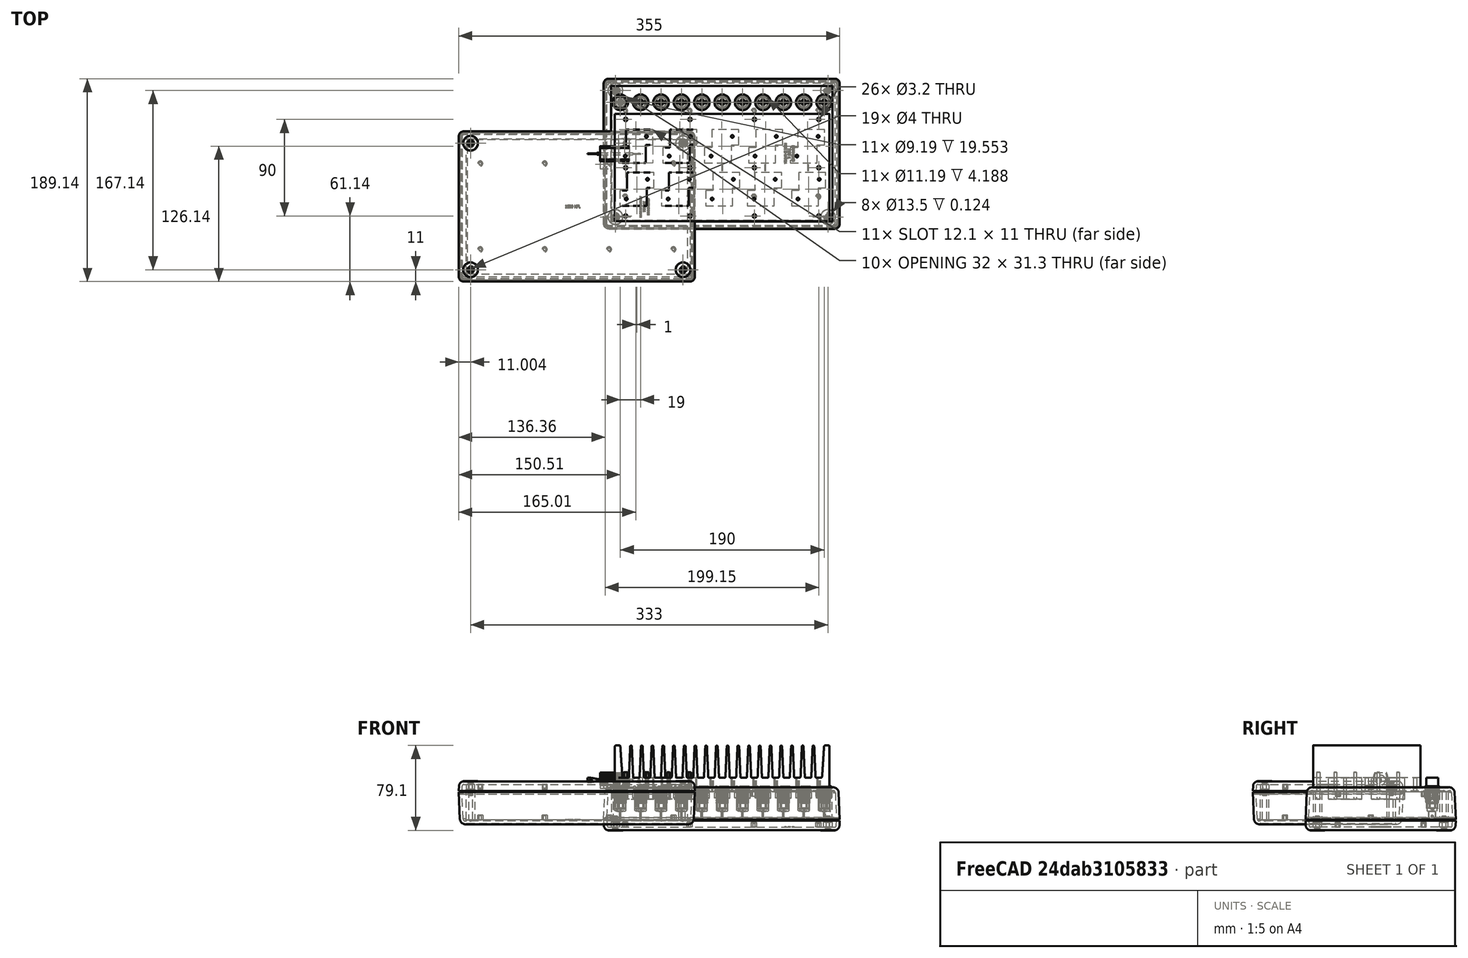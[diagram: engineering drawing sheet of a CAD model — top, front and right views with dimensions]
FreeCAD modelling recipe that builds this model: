
FCSTD DOCUMENT  (FreeCAD 0.20R29410 (Git))
Label: LiPoKiller - Kopie
License: All rights reserved
LicenseURL: http://en.wikipedia.org/wiki/All_rights_reserved
objects: Part::Feature×32, Part::FeaturePython×17, Sketcher::SketchObject×10, Part::Extrusion×10, App::Part×6, Part::MultiFuse×4, Part::Cut×3, App::DocumentObjectGroup×2, Spreadsheet::Sheet×1, PartDesign::CoordinateSystem×1, App::FeaturePython×1
note: 62 computed .brp shape members not serialized (recipe doc carries the construction recipe); baked Part::Feature solids carry a one-line shape summary decoded from their .brp

FEATURE [Spreadsheet::Sheet] Spreadsheet  label="Param"
  cells = A1=R_Grid_Along; B1(R_Grid_Along)=40; A2=R_Grid_Across; B2(R_Grid_Across)=40; A3=R_nof_Along; B3(R_nof_Along)=2; A4=R_nof_Across; B4(R_nof_Across)=5; A5=R_Offset; B5(R_Offset)=1; A6=R_Body_Length; B6(R_Body_Length)=27.3; A7=R_Body_Width; B7(R_Body_Width)=14.2; A8=R_Tab_Length; B8(R_Tab_Length)=10.4; A9=R_Tab_Width; B9(R_Tab_Width)==(28 - 14.2) / 2; A10=R_Clearance; B10(R_Clearance)=2; A11=R_Hole_Along; B11(R_Hole_Along)=18.3; A12=R_Hole_Across; B12(R_Hole_Across)=19.8; A13=R_Hole_Size; B13(R_Hole_Size)=2.5; A14=R_Thread; B14(R_Thread)=M3; A15=Heatsink_Length; B15(Heatsink_Length)=200; A16=Heatsing_Width; B16(Heatsink_Width)=100; A17=Heatsink_Shift; B17(Heatsink_Shift)==26 / 2; A18=Con_Grid; B18(Con_Grid)=19; A19=Con_Pos_y; B19(Con_Pos_y)=48; A20=Con_nof; B20(Con_nof)=11; A21=Con_Diameter; B21(Con_Diameter)=12.1; A22=Con_Width; B22(Con_Width)=11; A23=Heatsink_Hole; B23(Heatsink_Hole)=3.2; C23=Change to 2.5 before manufacturing heatsink; A24=Heatsink_Thread_Hole; B24(Heatsink_Thread_Hole)=2.5; A25=Heatsink_Thread; B25(Heatsink_Thread)=M3; A26=Heatsink_Hole_nof_x; B26(Heatsink_Hole_nof_x)=4; A27=Heatsink_Hole_nof_y; B27(Heatsink_Hole_nof_y)=3; A28=Heatsink_Hole_Grid_x; B28(Heatsink_Hole_Grid_x)=60; A29=Heatsink_Hole_Grid_y; B29(Heatsink_Hole_Grid_y)=45; A30=Heatsink_Hole_Offset; B30(Heatsink_Hole_Offset)=5
FEATURE [Sketcher::SketchObject] Sketch
  FullyConstrained = true
  expr: Constraints[10] = <<Param>>.R_Tab_Width
  expr: Constraints[11] = <<Param>>.R_Tab_Width
  expr: Constraints[12] = <<Param>>.R_Tab_Length + 2 * <<Param>>.R_Clearance
  expr: Constraints[13] = <<Param>>.R_Tab_Length + 2 * <<Param>>.R_Clearance
  expr: Constraints[20] = <<Param>>.R_Grid_Along * (<<Param>>.R_nof_Along - 1) / 2 + <<Param>>.Heatsink_Shift
  expr: Constraints[29] = <<Param>>.Heatsink_Length / 2 - <<Param>>.R_Grid_Across * (<<Param>>.R_nof_Across - 1) / 2 + <<Param>>.R_Offset / 2
  expr: Constraints[8] = Spreadsheet.R_Body_Width + 2 * <<Param>>.R_Clearance
  expr: Constraints[9] = <<Param>>.R_Body_Length + 2 * <<Param>>.R_Clearance
  sketch-geometry (11):
    g0: LineSegment StartX=4.5 StartY=-48.65 StartZ=0 EndX=29.6 EndY=-48.65 EndZ=0
    g1: LineSegment StartX=29.6 StartY=-48.65 StartZ=0 EndX=29.6 EndY=-31.75 EndZ=0
    g2: LineSegment StartX=29.6 StartY=-31.75 StartZ=0 EndX=36.5 EndY=-31.75 EndZ=0
    g3: LineSegment StartX=36.5 StartY=-31.75 StartZ=0 EndX=36.5 EndY=-17.35 EndZ=0
    g4: LineSegment StartX=36.5 StartY=-17.35 StartZ=0 EndX=11.4 EndY=-17.35 EndZ=0
    g5: LineSegment StartX=11.4 StartY=-17.35 StartZ=0 EndX=11.4 EndY=-34.25 EndZ=0
    g6: LineSegment StartX=11.4 StartY=-34.25 StartZ=0 EndX=4.5 EndY=-34.25 EndZ=0
    g7: LineSegment StartX=4.5 StartY=-34.25 StartZ=0 EndX=4.5 EndY=-48.65 EndZ=0
    g8: LineSegment StartX=11.4 StartY=-17.35 StartZ=0 EndX=29.6 EndY=-48.65 EndZ=0
    g9: LineSegment StartX=11.4 StartY=-34.25 StartZ=0 EndX=29.6 EndY=-31.75 EndZ=0
    g10: GeomPoint X=20.5 Y=-33 Z=0
  constraints (30):
    c: Coincident(g0,g1)
    c: Coincident(g1,g2)
    c: Coincident(g2,g3)
    c: Coincident(g3,g4)
    c: Coincident(g4,g5)
    c: Coincident(g5,g6)
    c: Coincident(g6,g7)
    c: Coincident(g7,g0)
    c: Distance(g5,g1) = 18.2
    c: Distance(g4,g0) = 31.3
    c: Distance(g6,g5) = 6.9
    c: Distance(g1,g2) = 6.9
    c: Distance(g3,g2) = 14.4
    c: Distance(g6,g0) = 14.4
    c: Coincident(g8,g4)
    c: Coincident(g9,g5)
    c: Coincident(g9,g1)
    c: Coincident(g8,g0)
    c: PointOnObject(g10,g9)
    c: PointOnObject(g10,g8)
    c: Distance(g10,g-1) = 33
    c: Perpendicular(g0,g7)
    c: Perpendicular(g0,g1)
    c: Perpendicular(g2,g1)
    c: Perpendicular(g2,g3)
    c: Perpendicular(g3,g4)
    c: Perpendicular(g4,g5)
    c: Perpendicular(g5,g6)
    c: Horizontal(g4)
    c: Distance(g10,g-2) = 20.5
FEATURE [Part::Extrusion] Extrude
  Base = -> Sketch
  Dir = (0,0,1)
  DirMode = 2
  FaceMakerClass = Part::FaceMakerBullseye
  LengthFwd = 10
  LengthRev = 10
  Solid = true
  Symmetric = false
FEATURE [Part::FeaturePython] Array001  # Draft array (typed FeaturePython)
  AlwaysSyncPlacement = false
  Angle = 360
  ArrayType = 0
  Axis = (0,0,1)
  Base = -> Extrude
  Center = (0,0,0)
  Count = 3
  ExpandArray = false
  Fuse = false
  IntervalAxis = (0,0,0)
  IntervalX = (80,0,0)
  IntervalY = (0,80,0)
  IntervalZ = (0,0,0)
  NumberCircles = 3
  NumberPolar = 5
  NumberX = 3
  NumberY = 1
  NumberZ = 1
  PlacementList = 3 placements: arithmetic series from (0,0,0) step (80,0,0) to (160,0,0)
  RadialDistance = 50
  ScaleList = (3) [(1,1,1),(1,1,1),(1,1,1)]
  Symmetry = 1
  TangentialDistance = 25
  expr: .IntervalX.x = <<Param>>.R_Grid_Across * 2
  expr: .IntervalY.y = <<Param>>.R_Grid_Along * 2
  expr: NumberX = ceil(<<Param>>.R_nof_Across / 2)
  expr: NumberY = ceil(<<Param>>.R_nof_Along / 2)
FEATURE [Sketcher::SketchObject] Sketch001
  FullyConstrained = true
  expr: Constraints[10] = <<Param>>.R_Tab_Width
  expr: Constraints[11] = <<Param>>.R_Tab_Width
  expr: Constraints[12] = <<Param>>.R_Tab_Length + 2 * <<Param>>.R_Clearance
  expr: Constraints[13] = <<Param>>.R_Tab_Length + 2 * <<Param>>.R_Clearance
  expr: Constraints[20] = <<Param>>.R_Grid_Along * (<<Param>>.R_nof_Along - 1) / 2 + <<Param>>.Heatsink_Shift
  expr: Constraints[29] = <<Param>>.Heatsink_Length / 2 - <<Param>>.R_Grid_Across * (<<Param>>.R_nof_Across - 3) / 2 - <<Param>>.R_Offset / 2
  expr: Constraints[8] = Spreadsheet.R_Body_Width + 2 * <<Param>>.R_Clearance
  expr: Constraints[9] = <<Param>>.R_Body_Length + 2 * <<Param>>.R_Clearance
  sketch-geometry (11):
    g0: LineSegment StartX=43.5 StartY=-48.65 StartZ=0 EndX=68.6 EndY=-48.65 EndZ=0
    g1: LineSegment StartX=68.6 StartY=-48.65 StartZ=0 EndX=68.6 EndY=-31.75 EndZ=0
    g2: LineSegment StartX=68.6 StartY=-31.75 StartZ=0 EndX=75.5 EndY=-31.75 EndZ=0
    g3: LineSegment StartX=75.5 StartY=-31.75 StartZ=0 EndX=75.5 EndY=-17.35 EndZ=0
    g4: LineSegment StartX=75.5 StartY=-17.35 StartZ=0 EndX=50.4 EndY=-17.35 EndZ=0
    g5: LineSegment StartX=50.4 StartY=-17.35 StartZ=0 EndX=50.4 EndY=-34.25 EndZ=0
    g6: LineSegment StartX=50.4 StartY=-34.25 StartZ=0 EndX=43.5 EndY=-34.25 EndZ=0
    g7: LineSegment StartX=43.5 StartY=-34.25 StartZ=0 EndX=43.5 EndY=-48.65 EndZ=0
    g8: LineSegment StartX=50.4 StartY=-17.35 StartZ=0 EndX=68.6 EndY=-48.65 EndZ=0
    g9: LineSegment StartX=50.4 StartY=-34.25 StartZ=0 EndX=68.6 EndY=-31.75 EndZ=0
    g10: GeomPoint X=59.5 Y=-33 Z=0
  constraints (30):
    c: Coincident(g0,g1)
    c: Coincident(g1,g2)
    c: Coincident(g2,g3)
    c: Coincident(g3,g4)
    c: Coincident(g4,g5)
    c: Coincident(g5,g6)
    c: Coincident(g6,g7)
    c: Coincident(g7,g0)
    c: Distance(g5,g1) = 18.2
    c: Distance(g4,g0) = 31.3
    c: Distance(g6,g5) = 6.9
    c: Distance(g1,g2) = 6.9
    c: Distance(g3,g2) = 14.4
    c: Distance(g6,g0) = 14.4
    c: Coincident(g8,g4)
    c: Coincident(g9,g5)
    c: Coincident(g9,g1)
    c: Coincident(g8,g0)
    c: PointOnObject(g10,g9)
    c: PointOnObject(g10,g8)
    c: Distance(g10,g-1) = 33
    c: Perpendicular(g0,g7)
    c: Perpendicular(g0,g1)
    c: Perpendicular(g2,g1)
    c: Perpendicular(g2,g3)
    c: Perpendicular(g3,g4)
    c: Perpendicular(g4,g5)
    c: Perpendicular(g5,g6)
    c: Horizontal(g4)
    c: Distance(g10,g-2) = 59.5
FEATURE [Part::Extrusion] Extrude001
  Base = -> Sketch001
  Dir = (0,0,1)
  DirMode = 2
  FaceMakerClass = Part::FaceMakerBullseye
  LengthFwd = 10
  LengthRev = 10
  Solid = true
  Symmetric = false
FEATURE [Part::FeaturePython] Array002  # Draft array (typed FeaturePython)
  AlwaysSyncPlacement = false
  Angle = 360
  ArrayType = 0
  Axis = (0,0,1)
  Base = -> Extrude001
  Center = (0,0,0)
  Count = 2
  ExpandArray = false
  Fuse = false
  IntervalAxis = (0,0,0)
  IntervalX = (80,0,0)
  IntervalY = (0,80,0)
  IntervalZ = (0,0,0)
  NumberCircles = 3
  NumberPolar = 5
  NumberX = 2
  NumberY = 1
  NumberZ = 1
  PlacementList = 2 placements: [(0,0,0),(80,0,0)]
  RadialDistance = 50
  ScaleList = (2) [(1,1,1),(1,1,1)]
  Symmetry = 1
  TangentialDistance = 25
  expr: .IntervalX.x = <<Param>>.R_Grid_Across * 2
  expr: .IntervalY.y = <<Param>>.R_Grid_Along * 2
  expr: NumberX = floor(<<Param>>.R_nof_Across / 2)
  expr: NumberY = floor(<<Param>>.R_nof_Along / 2)
FEATURE [Sketcher::SketchObject] Sketch002
  FullyConstrained = true
  expr: Constraints[10] = <<Param>>.R_Tab_Width
  expr: Constraints[11] = <<Param>>.R_Tab_Width
  expr: Constraints[12] = <<Param>>.R_Tab_Length + 2 * <<Param>>.R_Clearance
  expr: Constraints[13] = <<Param>>.R_Tab_Length + 2 * <<Param>>.R_Clearance
  expr: Constraints[28] = <<Param>>.Heatsink_Length / 2 - <<Param>>.R_Grid_Across * (<<Param>>.R_nof_Across - 1) / 2 - <<Param>>.R_Offset / 2
  expr: Constraints[31] = <<Param>>.R_Grid_Along * (<<Param>>.R_nof_Along - 1) / 2 + <<Param>>.Heatsink_Shift
  expr: Constraints[33] = <<Param>>.R_Grid_Along
  expr: Constraints[8] = Spreadsheet.R_Body_Width + 2 * <<Param>>.R_Clearance
  expr: Constraints[9] = <<Param>>.R_Body_Length + 2 * <<Param>>.R_Clearance
  sketch-geometry (12):
    g0: LineSegment StartX=3.5 StartY=-8.65 StartZ=0 EndX=28.6 EndY=-8.65 EndZ=0
    g1: LineSegment StartX=28.6 StartY=-8.65 StartZ=0 EndX=28.6 EndY=8.25 EndZ=0
    g2: LineSegment StartX=28.6 StartY=8.25 StartZ=0 EndX=35.5 EndY=8.25 EndZ=0
    g3: LineSegment StartX=35.5 StartY=8.25 StartZ=0 EndX=35.5 EndY=22.65 EndZ=0
    g4: LineSegment StartX=35.5 StartY=22.65 StartZ=0 EndX=10.4 EndY=22.65 EndZ=0
    g5: LineSegment StartX=10.4 StartY=22.65 StartZ=0 EndX=10.4 EndY=5.75 EndZ=0
    g6: LineSegment StartX=10.4 StartY=5.75 StartZ=0 EndX=3.5 EndY=5.75 EndZ=0
    g7: LineSegment StartX=3.5 StartY=5.75 StartZ=0 EndX=3.5 EndY=-8.65 EndZ=0
    g8: LineSegment StartX=10.4 StartY=22.65 StartZ=0 EndX=28.6 EndY=-8.65 EndZ=0
    g9: LineSegment StartX=10.4 StartY=5.75 StartZ=0 EndX=28.6 EndY=8.25 EndZ=0
    g10: GeomPoint X=19.5 Y=7 Z=0
    g11: LineSegment StartX=0 StartY=-33 StartZ=0 EndX=200 EndY=-33 EndZ=0
  constraints (34):
    c: Coincident(g0,g1)
    c: Coincident(g1,g2)
    c: Coincident(g2,g3)
    c: Coincident(g3,g4)
    c: Coincident(g4,g5)
    c: Coincident(g5,g6)
    c: Coincident(g6,g7)
    c: Coincident(g7,g0)
    c: Distance(g5,g1) = 18.2
    c: Distance(g4,g0) = 31.3
    c: Distance(g6,g5) = 6.9
    c: Distance(g1,g2) = 6.9
    c: Distance(g3,g2) = 14.4
    c: Distance(g6,g0) = 14.4
    c: Coincident(g8,g4)
    c: Coincident(g9,g5)
    c: Coincident(g9,g1)
    c: Coincident(g8,g0)
    c: PointOnObject(g10,g9)
    c: PointOnObject(g10,g8)
    c: Perpendicular(g0,g7)
    c: Perpendicular(g0,g1)
    c: Perpendicular(g2,g1)
    c: Perpendicular(g2,g3)
    c: Perpendicular(g3,g4)
    c: Perpendicular(g4,g5)
    c: Perpendicular(g5,g6)
    c: Horizontal(g4)
    c: Distance(g10,g-2) = 19.5
    c: PointOnObject(g11,g-2)
    c: Horizontal(g11)
    c: Distance(g11,g-1) = 33
    c: Distance(g11,g-2) = 200
    c: Distance(g10,g11) = 40
FEATURE [Part::Extrusion] Extrude002
  Base = -> Sketch002
  Dir = (0,0,1)
  DirMode = 2
  FaceMakerClass = Part::FaceMakerBullseye
  LengthFwd = 10
  LengthRev = 10
  Solid = true
  Symmetric = false
FEATURE [Part::FeaturePython] Array003  # Draft array (typed FeaturePython)
  AlwaysSyncPlacement = false
  Angle = 360
  ArrayType = 0
  Axis = (0,0,1)
  Base = -> Extrude002
  Center = (0,0,0)
  Count = 3
  ExpandArray = false
  Fuse = false
  IntervalAxis = (0,0,0)
  IntervalX = (80,0,0)
  IntervalY = (0,80,0)
  IntervalZ = (0,0,0)
  NumberCircles = 3
  NumberPolar = 5
  NumberX = 3
  NumberY = 1
  NumberZ = 1
  PlacementList = 3 placements: arithmetic series from (0,0,0) step (80,0,0) to (160,0,0)
  RadialDistance = 50
  ScaleList = (3) [(1,1,1),(1,1,1),(1,1,1)]
  Symmetry = 1
  TangentialDistance = 25
  expr: .IntervalX.x = <<Param>>.R_Grid_Across * 2
  expr: .IntervalY.y = <<Param>>.R_Grid_Along * 2
  expr: NumberX = ceil(<<Param>>.R_nof_Across / 2)
  expr: NumberY = floor(<<Param>>.R_nof_Along / 2)
FEATURE [Sketcher::SketchObject] Sketch003
  FullyConstrained = true
  expr: Constraints[10] = <<Param>>.R_Tab_Width
  expr: Constraints[11] = <<Param>>.R_Tab_Width
  expr: Constraints[12] = <<Param>>.R_Tab_Length + 2 * <<Param>>.R_Clearance
  expr: Constraints[13] = <<Param>>.R_Tab_Length + 2 * <<Param>>.R_Clearance
  expr: Constraints[28] = <<Param>>.Heatsink_Length / 2 - <<Param>>.R_Grid_Across * (<<Param>>.R_nof_Across - 3) / 2 + <<Param>>.R_Offset / 2
  expr: Constraints[31] = <<Param>>.R_Grid_Along * (<<Param>>.R_nof_Along - 1) / 2 + <<Param>>.Heatsink_Shift
  expr: Constraints[33] = <<Param>>.R_Grid_Along
  expr: Constraints[8] = Spreadsheet.R_Body_Width + 2 * <<Param>>.R_Clearance
  expr: Constraints[9] = <<Param>>.R_Body_Length + 2 * <<Param>>.R_Clearance
  sketch-geometry (12):
    g0: LineSegment StartX=44.5 StartY=-8.65 StartZ=0 EndX=69.6 EndY=-8.65 EndZ=0
    g1: LineSegment StartX=69.6 StartY=-8.65 StartZ=0 EndX=69.6 EndY=8.25 EndZ=0
    g2: LineSegment StartX=69.6 StartY=8.25 StartZ=0 EndX=76.5 EndY=8.25 EndZ=0
    g3: LineSegment StartX=76.5 StartY=8.25 StartZ=0 EndX=76.5 EndY=22.65 EndZ=0
    g4: LineSegment StartX=76.5 StartY=22.65 StartZ=0 EndX=51.4 EndY=22.65 EndZ=0
    g5: LineSegment StartX=51.4 StartY=22.65 StartZ=0 EndX=51.4 EndY=5.75 EndZ=0
    g6: LineSegment StartX=51.4 StartY=5.75 StartZ=0 EndX=44.5 EndY=5.75 EndZ=0
    g7: LineSegment StartX=44.5 StartY=5.75 StartZ=0 EndX=44.5 EndY=-8.65 EndZ=0
    g8: LineSegment StartX=51.4 StartY=22.65 StartZ=0 EndX=69.6 EndY=-8.65 EndZ=0
    g9: LineSegment StartX=51.4 StartY=5.75 StartZ=0 EndX=69.6 EndY=8.25 EndZ=0
    g10: GeomPoint X=60.5 Y=7 Z=0
    g11: LineSegment StartX=0 StartY=-33 StartZ=0 EndX=200 EndY=-33 EndZ=0
  constraints (34):
    c: Coincident(g0,g1)
    c: Coincident(g1,g2)
    c: Coincident(g2,g3)
    c: Coincident(g3,g4)
    c: Coincident(g4,g5)
    c: Coincident(g5,g6)
    c: Coincident(g6,g7)
    c: Coincident(g7,g0)
    c: Distance(g5,g1) = 18.2
    c: Distance(g4,g0) = 31.3
    c: Distance(g6,g5) = 6.9
    c: Distance(g1,g2) = 6.9
    c: Distance(g3,g2) = 14.4
    c: Distance(g6,g0) = 14.4
    c: Coincident(g8,g4)
    c: Coincident(g9,g5)
    c: Coincident(g9,g1)
    c: Coincident(g8,g0)
    c: PointOnObject(g10,g9)
    c: PointOnObject(g10,g8)
    c: Perpendicular(g0,g7)
    c: Perpendicular(g0,g1)
    c: Perpendicular(g2,g1)
    c: Perpendicular(g2,g3)
    c: Perpendicular(g3,g4)
    c: Perpendicular(g4,g5)
    c: Perpendicular(g5,g6)
    c: Horizontal(g4)
    c: Distance(g10,g-2) = 60.5
    c: PointOnObject(g11,g-2)
    c: Horizontal(g11)
    c: Distance(g11,g-1) = 33
    c: Distance(g11,g-2) = 200
    c: Distance(g10,g11) = 40
FEATURE [Part::Extrusion] Extrude003
  Base = -> Sketch003
  Dir = (0,0,1)
  DirMode = 2
  FaceMakerClass = Part::FaceMakerBullseye
  LengthFwd = 10
  LengthRev = 10
  Solid = true
  Symmetric = false
FEATURE [Part::FeaturePython] Array004  # Draft array (typed FeaturePython)
  AlwaysSyncPlacement = false
  Angle = 360
  ArrayType = 0
  Axis = (0,0,1)
  Base = -> Extrude003
  Center = (0,0,0)
  Count = 2
  ExpandArray = false
  Fuse = false
  IntervalAxis = (0,0,0)
  IntervalX = (80,0,0)
  IntervalY = (0,80,0)
  IntervalZ = (0,0,0)
  NumberCircles = 3
  NumberPolar = 5
  NumberX = 2
  NumberY = 1
  NumberZ = 1
  PlacementList = 2 placements: [(0,0,0),(80,0,0)]
  RadialDistance = 50
  ScaleList = (2) [(1,1,1),(1,1,1)]
  Symmetry = 1
  TangentialDistance = 25
  expr: .IntervalX.x = <<Param>>.R_Grid_Across * 2
  expr: .IntervalY.y = <<Param>>.R_Grid_Along * 2
  expr: NumberX = floor(<<Param>>.R_nof_Across / 2)
  expr: NumberY = floor(<<Param>>.R_nof_Along / 2)
FEATURE [Part::Feature] Part__Feature012  label="Resistor Arcol HS"
  shape: bbox 27.3 x 28 x 14.8 mm, 83 faces (baked)
FEATURE [Part::Feature] Part__Feature013  label="Resistor Arcol HS001"
  shape: bbox 33.3 x 2.1 x 2.1 mm, 3 faces (baked)
FEATURE [Part::Feature] Part__Feature014  label="Resistor Arcol HS002"
  shape: bbox 8.85 x 0.8 x 4.5 mm, 7 faces (baked)
FEATURE [Part::Feature] Part__Feature015  label="Resistor Arcol HS003"
  shape: bbox 8.85 x 0.8 x 4.5 mm, 7 faces (baked)
FEATURE [Part::Feature] Part__Feature016  label="Resistor Arcol HS004"
  shape: bbox 27.3 x 9.23 x 9.23 mm, 6 faces, 0 solids (baked)
FEATURE [App::Part] Resistor_Arcol_HS  label="Resistor Arcol HS005"
  Group = -> [Part__Feature012,Part__Feature013,Part__Feature014,Part__Feature015,Part__Feature016]
  Origin = -> Origin002
  Placement = pos=(20.5,-33,2.8e-15) rot=(0.707107,0.707107,0;3.14159rad)
  expr: .Placement.Base.x = <<Param>>.Heatsink_Length / 2 - <<Param>>.R_Grid_Across * (<<Param>>.R_nof_Across - 1) / 2 + <<Param>>.R_Offset / 2
  expr: .Placement.Base.y = -(<<Param>>.R_Grid_Along * (<<Param>>.R_nof_Along - 1) / 2 + <<Param>>.Heatsink_Shift)
FEATURE [Part::FeaturePython] Array005  # Draft array (typed FeaturePython)
  AlwaysSyncPlacement = false
  Angle = 360
  ArrayType = 0
  Axis = (0,0,1)
  Base = -> Resistor_Arcol_HS
  Center = (0,0,0)
  Count = 3
  ExpandArray = false
  Fuse = false
  IntervalAxis = (0,0,0)
  IntervalX = (80,0,0)
  IntervalY = (0,80,0)
  IntervalZ = (0,0,0)
  NumberCircles = 3
  NumberPolar = 5
  NumberX = 3
  NumberY = 1
  NumberZ = 1
  PlacementList = 3 placements: arithmetic series from (20.5,-33,2.8e-15) step (80,0,0) to (180.5,-33,2.8e-15)
  RadialDistance = 50
  ScaleList = (3) [(1,1,1),(1,1,1),(1,1,1)]
  Symmetry = 1
  TangentialDistance = 25
  expr: .IntervalX.x = <<Param>>.R_Grid_Across * 2
  expr: .IntervalY.y = <<Param>>.R_Grid_Along * 2
  expr: NumberX = ceil(<<Param>>.R_nof_Across / 2)
  expr: NumberY = ceil(<<Param>>.R_nof_Along / 2)
FEATURE [Part::Feature] Part__Feature017  label="Resistor Arcol HS006"
  shape: bbox 27.3 x 28 x 14.8 mm, 83 faces (baked)
FEATURE [Part::Feature] Part__Feature018  label="Resistor Arcol HS007"
  shape: bbox 33.3 x 2.1 x 2.1 mm, 3 faces (baked)
FEATURE [Part::Feature] Part__Feature019  label="Resistor Arcol HS008"
  shape: bbox 8.85 x 0.8 x 4.5 mm, 7 faces (baked)
FEATURE [Part::Feature] Part__Feature020  label="Resistor Arcol HS009"
  shape: bbox 8.85 x 0.8 x 4.5 mm, 7 faces (baked)
FEATURE [Part::Feature] Part__Feature021  label="Resistor Arcol HS010"
  shape: bbox 27.3 x 9.23 x 9.23 mm, 6 faces, 0 solids (baked)
FEATURE [App::Part] Resistor_Arcol_HS001  label="Resistor Arcol HS011"
  Group = -> [Part__Feature017,Part__Feature018,Part__Feature019,Part__Feature020,Part__Feature021]
  Origin = -> Origin003
  Placement = pos=(59.5,-33,2.8e-15) rot=(0.707107,0.707107,0;3.14159rad)
  expr: .Placement.Base.x = <<Param>>.Heatsink_Length / 2 - <<Param>>.R_Grid_Across * (<<Param>>.R_nof_Across - 3) / 2 - <<Param>>.R_Offset / 2
  expr: .Placement.Base.y = -(<<Param>>.R_Grid_Along * (<<Param>>.R_nof_Along - 1) / 2 + <<Param>>.Heatsink_Shift)
FEATURE [Part::FeaturePython] Array006  # Draft array (typed FeaturePython)
  AlwaysSyncPlacement = false
  Angle = 360
  ArrayType = 0
  Axis = (0,0,1)
  Base = -> Resistor_Arcol_HS001
  Center = (0,0,0)
  Count = 2
  ExpandArray = false
  Fuse = false
  IntervalAxis = (0,0,0)
  IntervalX = (80,0,0)
  IntervalY = (0,80,0)
  IntervalZ = (0,0,0)
  NumberCircles = 3
  NumberPolar = 5
  NumberX = 2
  NumberY = 1
  NumberZ = 1
  PlacementList = 2 placements: [(59.5,-33,2.8e-15),(139.5,-33,2.8e-15)]
  RadialDistance = 50
  ScaleList = (2) [(1,1,1),(1,1,1)]
  Symmetry = 1
  TangentialDistance = 25
  expr: .IntervalX.x = <<Param>>.R_Grid_Across * 2
  expr: .IntervalY.y = <<Param>>.R_Grid_Along * 2
  expr: NumberX = floor(<<Param>>.R_nof_Across / 2)
  expr: NumberY = floor(<<Param>>.R_nof_Along / 2)
FEATURE [Part::Feature] Part__Feature022  label="Resistor Arcol HS012"
  shape: bbox 27.3 x 28 x 14.8 mm, 83 faces (baked)
FEATURE [Part::Feature] Part__Feature023  label="Resistor Arcol HS013"
  shape: bbox 33.3 x 2.1 x 2.1 mm, 3 faces (baked)
FEATURE [Part::Feature] Part__Feature024  label="Resistor Arcol HS014"
  shape: bbox 8.85 x 0.8 x 4.5 mm, 7 faces (baked)
FEATURE [Part::Feature] Part__Feature025  label="Resistor Arcol HS015"
  shape: bbox 8.85 x 0.8 x 4.5 mm, 7 faces (baked)
FEATURE [Part::Feature] Part__Feature026  label="Resistor Arcol HS016"
  shape: bbox 27.3 x 9.23 x 9.23 mm, 6 faces, 0 solids (baked)
FEATURE [App::Part] Resistor_Arcol_HS002  label="Resistor Arcol HS017"
  Group = -> [Part__Feature022,Part__Feature023,Part__Feature024,Part__Feature025,Part__Feature026]
  Origin = -> Origin004
  Placement = pos=(19.5,7,2.8e-15) rot=(0.707107,0.707107,0;3.14159rad)
  expr: .Placement.Base.x = <<Param>>.Heatsink_Length / 2 - <<Param>>.R_Grid_Across * (<<Param>>.R_nof_Across - 1) / 2 - <<Param>>.R_Offset / 2
  expr: .Placement.Base.y = -(<<Param>>.R_Grid_Along * (<<Param>>.R_nof_Along - 1) / 2 + <<Param>>.Heatsink_Shift) + <<Param>>.R_Grid_Along
FEATURE [Part::FeaturePython] Array007  # Draft array (typed FeaturePython)
  AlwaysSyncPlacement = false
  Angle = 360
  ArrayType = 0
  Axis = (0,0,1)
  Base = -> Resistor_Arcol_HS002
  Center = (0,0,0)
  Count = 3
  ExpandArray = false
  Fuse = false
  IntervalAxis = (0,0,0)
  IntervalX = (80,0,0)
  IntervalY = (0,80,0)
  IntervalZ = (0,0,0)
  NumberCircles = 3
  NumberPolar = 5
  NumberX = 3
  NumberY = 1
  NumberZ = 1
  PlacementList = 3 placements: arithmetic series from (19.5,7,2.8e-15) step (80,0,0) to (179.5,7,2.8e-15)
  RadialDistance = 50
  ScaleList = (3) [(1,1,1),(1,1,1),(1,1,1)]
  Symmetry = 1
  TangentialDistance = 25
  expr: .IntervalX.x = <<Param>>.R_Grid_Across * 2
  expr: .IntervalY.y = <<Param>>.R_Grid_Along * 2
  expr: NumberX = ceil(<<Param>>.R_nof_Across / 2)
  expr: NumberY = floor(<<Param>>.R_nof_Along / 2)
FEATURE [Part::Feature] Part__Feature027  label="Resistor Arcol HS018"
  shape: bbox 27.3 x 28 x 14.8 mm, 83 faces (baked)
FEATURE [Part::Feature] Part__Feature028  label="Resistor Arcol HS019"
  shape: bbox 33.3 x 2.1 x 2.1 mm, 3 faces (baked)
FEATURE [Part::Feature] Part__Feature029  label="Resistor Arcol HS020"
  shape: bbox 8.85 x 0.8 x 4.5 mm, 7 faces (baked)
FEATURE [Part::Feature] Part__Feature030  label="Resistor Arcol HS021"
  shape: bbox 8.85 x 0.8 x 4.5 mm, 7 faces (baked)
FEATURE [Part::Feature] Part__Feature031  label="Resistor Arcol HS022"
  shape: bbox 27.3 x 9.23 x 9.23 mm, 6 faces, 0 solids (baked)
FEATURE [App::Part] Resistor_Arcol_HS003  label="Resistor Arcol HS023"
  Group = -> [Part__Feature027,Part__Feature028,Part__Feature029,Part__Feature030,Part__Feature031]
  Origin = -> Origin005
  Placement = pos=(60.5,7,2.8e-15) rot=(0.707107,0.707107,0;3.14159rad)
  expr: .Placement.Base.x = <<Param>>.Heatsink_Length / 2 - <<Param>>.R_Grid_Across * (<<Param>>.R_nof_Across - 3) / 2 + <<Param>>.R_Offset / 2
  expr: .Placement.Base.y = -(<<Param>>.R_Grid_Along * (<<Param>>.R_nof_Along - 1) / 2 + <<Param>>.Heatsink_Shift) + <<Param>>.R_Grid_Along
FEATURE [Part::FeaturePython] Array008  # Draft array (typed FeaturePython)
  AlwaysSyncPlacement = false
  Angle = 360
  ArrayType = 0
  Axis = (0,0,1)
  Base = -> Resistor_Arcol_HS003
  Center = (0,0,0)
  Count = 2
  ExpandArray = false
  Fuse = false
  IntervalAxis = (0,0,0)
  IntervalX = (80,0,0)
  IntervalY = (0,80,0)
  IntervalZ = (0,0,0)
  NumberCircles = 3
  NumberPolar = 5
  NumberX = 2
  NumberY = 1
  NumberZ = 1
  PlacementList = 2 placements: [(60.5,7,2.8e-15),(140.5,7,2.8e-15)]
  RadialDistance = 50
  ScaleList = (2) [(1,1,1),(1,1,1)]
  Symmetry = 1
  TangentialDistance = 25
  expr: .IntervalX.x = <<Param>>.R_Grid_Across * 2
  expr: .IntervalY.y = <<Param>>.R_Grid_Along * 2
  expr: NumberX = floor(<<Param>>.R_nof_Across / 2)
  expr: NumberY = floor(<<Param>>.R_nof_Along / 2)
FEATURE [Part::MultiFuse] Fusion
  Shapes = -> [Array001,Array002,Array003,Array004]
FEATURE [Sketcher::SketchObject] Sketch004
  FullyConstrained = true
  expr: Constraints[10] = <<Param>>.Con_Pos_y
  expr: Constraints[12] = <<Param>>.Heatsink_Length / 2 - <<Param>>.Con_Grid * (<<Param>>.Con_nof - 1) / 2
  expr: Constraints[6] = <<Param>>.Con_Diameter
  expr: Constraints[7] = <<Param>>.Con_Diameter
  expr: Constraints[8] = <<Param>>.Con_Width
  expr: Constraints[9] = <<Param>>.Con_Width / 2
  sketch-geometry (4):
    g0: ArcOfCircle CenterX=5 CenterY=48 CenterZ=0 NormalX=0 NormalY=0 NormalZ=1 AngleXU=0 Radius=6.05 StartAngle=2.0005 EndAngle=4.28269
    g1: ArcOfCircle CenterX=5 CenterY=48 CenterZ=0 NormalX=0 NormalY=0 NormalZ=1 AngleXU=0 Radius=6.05 StartAngle=5.14209 EndAngle=7.42428
    g2: LineSegment StartX=2.47958 StartY=53.5 StartZ=0 EndX=7.52042 EndY=53.5 EndZ=0
    g3: LineSegment StartX=7.52042 StartY=42.5 StartZ=0 EndX=2.47958 EndY=42.5 EndZ=0
  constraints (13):
    c: Coincident(g1,g0)
    c: Coincident(g2,g0)
    c: Coincident(g2,g1)
    c: Coincident(g3,g1)
    c: Coincident(g3,g0)
    c: Horizontal(g3)
    c: Diameter(g1) = 12.1
    c: Diameter(g0) = 12.1
    c: Distance(g1,g3) = 11
    c: Distance(g0,g3) = 5.5
    c: Distance(g0,g-1) = 48
    c: Horizontal(g2)
    c: Distance(g0,g-2) = 5
FEATURE [Part::Extrusion] Extrude004
  Base = -> Sketch004
  Dir = (0,0,1)
  DirMode = 2
  FaceMakerClass = Part::FaceMakerBullseye
  LengthFwd = 10
  LengthRev = 10
  Solid = true
  Symmetric = false
FEATURE [Part::FeaturePython] Array009  # Draft array (typed FeaturePython)
  AlwaysSyncPlacement = false
  Angle = 360
  ArrayType = 0
  Axis = (0,0,1)
  Base = -> Extrude004
  Center = (0,0,0)
  Count = 11
  ExpandArray = false
  Fuse = false
  IntervalAxis = (0,0,0)
  IntervalX = (19,0,0)
  IntervalY = (0,100,0)
  IntervalZ = (0,0,100)
  NumberCircles = 3
  NumberPolar = 5
  NumberX = 11
  NumberY = 1
  NumberZ = 1
  PlacementList = 11 placements: arithmetic series from (0,0,0) step (19,0,0) to (190,0,0)
  RadialDistance = 50
  ScaleList = (11) [(1,1,1),(1,1,1),(1,1,1),(1,1,1),(1,1,1),(1,1,1),(1,1,1),(1,1,1),(1,1,1),(1,1,1),(1,1,1)]
  Symmetry = 1
  TangentialDistance = 25
FEATURE [Part::MultiFuse] Fusion001
  Shapes = -> [Array009,Fusion]
FEATURE [Sketcher::SketchObject] Sketch005
  FullyConstrained = true
  expr: Constraints[12] = <<Param>>.R_Hole_Size
  expr: Constraints[13] = <<Param>>.R_Hole_Size
  expr: Constraints[1] = <<Param>>.R_Grid_Along * (<<Param>>.R_nof_Along - 1) / 2 + <<Param>>.Heatsink_Shift
  expr: Constraints[2] = <<Param>>.Heatsink_Length / 2 - <<Param>>.R_Grid_Across * (<<Param>>.R_nof_Across - 1) / 2 + <<Param>>.R_Offset / 2
  expr: Constraints[5] = <<Param>>.R_Hole_Across
  expr: Constraints[6] = <<Param>>.R_Hole_Along
  sketch-geometry (6):
    g0: LineSegment StartX=30.4 StartY=-23.85 StartZ=0 EndX=10.6 EndY=-42.15 EndZ=0
    g1: GeomPoint X=20.5 Y=-33 Z=0
    g2: Circle CenterX=30.4 CenterY=-23.85 CenterZ=0 NormalX=0 NormalY=0 NormalZ=1 AngleXU=0 Radius=1.25
    g3: Circle CenterX=10.6 CenterY=-42.15 CenterZ=0 NormalX=0 NormalY=0 NormalZ=1 AngleXU=0 Radius=1.25
    g4: LineSegment StartX=20.5 StartY=-33 StartZ=0 EndX=30.4 EndY=-23.85 EndZ=0
    g5: LineSegment StartX=20.5 StartY=-33 StartZ=0 EndX=10.6 EndY=-42.15 EndZ=0
  constraints (14):
    c: PointOnObject(g1,g0)
    c: Distance(g1,g-1) = 33
    c: Distance(g1,g-2) = 20.5
    c: Coincident(g0,g2)
    c: Coincident(g0,g3)
    c: DistanceX(g3,g2) = 19.8
    c: DistanceY(g3,g2) = 18.3
    c: Coincident(g4,g1)
    c: Coincident(g4,g2)
    c: Coincident(g5,g1)
    c: Coincident(g5,g3)
    c: Equal(g4,g5)
    c: Diameter(g2) = 2.5
    c: Diameter(g3) = 2.5
FEATURE [Part::Extrusion] Extrude005
  Base = -> Sketch005
  Dir = (0,0,1)
  DirMode = 2
  FaceMakerClass = Part::FaceMakerBullseye
  LengthFwd = 15
  LengthRev = 10
  Solid = true
  Symmetric = false
FEATURE [Part::FeaturePython] Array010  # Draft array (typed FeaturePython)
  AlwaysSyncPlacement = false
  Angle = 360
  ArrayType = 0
  Axis = (0,0,1)
  Base = -> Extrude005
  Center = (0,0,0)
  Count = 3
  ExpandArray = false
  Fuse = false
  IntervalAxis = (0,0,0)
  IntervalX = (80,0,0)
  IntervalY = (0,80,0)
  IntervalZ = (0,0,0)
  NumberCircles = 3
  NumberPolar = 5
  NumberX = 3
  NumberY = 1
  NumberZ = 1
  PlacementList = 3 placements: arithmetic series from (0,0,0) step (80,0,0) to (160,0,0)
  RadialDistance = 50
  ScaleList = (3) [(1,1,1),(1,1,1),(1,1,1)]
  Symmetry = 1
  TangentialDistance = 25
  expr: .IntervalX.x = <<Param>>.R_Grid_Across * 2
  expr: .IntervalY.y = <<Param>>.R_Grid_Along * 2
  expr: NumberX = ceil(<<Param>>.R_nof_Across / 2)
  expr: NumberY = ceil(<<Param>>.R_nof_Along / 2)
FEATURE [Sketcher::SketchObject] Sketch006
  FullyConstrained = true
  expr: Constraints[12] = <<Param>>.R_Hole_Size
  expr: Constraints[13] = <<Param>>.R_Hole_Size
  expr: Constraints[1] = <<Param>>.R_Grid_Along * (<<Param>>.R_nof_Along - 1) / 2 + <<Param>>.Heatsink_Shift
  expr: Constraints[2] = <<Param>>.Heatsink_Length / 2 - <<Param>>.R_Grid_Across * (<<Param>>.R_nof_Across - 3) / 2 - <<Param>>.R_Offset / 2
  expr: Constraints[5] = <<Param>>.R_Hole_Across
  expr: Constraints[6] = <<Param>>.R_Hole_Along
  sketch-geometry (6):
    g0: LineSegment StartX=69.4 StartY=-23.85 StartZ=0 EndX=49.6 EndY=-42.15 EndZ=0
    g1: GeomPoint X=59.5 Y=-33 Z=0
    g2: Circle CenterX=69.4 CenterY=-23.85 CenterZ=0 NormalX=0 NormalY=0 NormalZ=1 AngleXU=0 Radius=1.25
    g3: Circle CenterX=49.6 CenterY=-42.15 CenterZ=0 NormalX=0 NormalY=0 NormalZ=1 AngleXU=0 Radius=1.25
    g4: LineSegment StartX=59.5 StartY=-33 StartZ=0 EndX=69.4 EndY=-23.85 EndZ=0
    g5: LineSegment StartX=59.5 StartY=-33 StartZ=0 EndX=49.6 EndY=-42.15 EndZ=0
  constraints (14):
    c: PointOnObject(g1,g0)
    c: Distance(g1,g-1) = 33
    c: Distance(g1,g-2) = 59.5
    c: Coincident(g0,g2)
    c: Coincident(g0,g3)
    c: DistanceX(g3,g2) = 19.8
    c: DistanceY(g3,g2) = 18.3
    c: Coincident(g4,g1)
    c: Coincident(g4,g2)
    c: Coincident(g5,g1)
    c: Coincident(g5,g3)
    c: Equal(g4,g5)
    c: Diameter(g2) = 2.5
    c: Diameter(g3) = 2.5
FEATURE [Part::Extrusion] Extrude006
  Base = -> Sketch006
  Dir = (0,0,1)
  DirMode = 2
  FaceMakerClass = Part::FaceMakerBullseye
  LengthFwd = 15
  LengthRev = 10
  Solid = true
  Symmetric = false
FEATURE [Part::FeaturePython] Array011  # Draft array (typed FeaturePython)
  AlwaysSyncPlacement = false
  Angle = 360
  ArrayType = 0
  Axis = (0,0,1)
  Base = -> Extrude006
  Center = (0,0,0)
  Count = 2
  ExpandArray = false
  Fuse = false
  IntervalAxis = (0,0,0)
  IntervalX = (80,0,0)
  IntervalY = (0,80,0)
  IntervalZ = (0,0,0)
  NumberCircles = 3
  NumberPolar = 5
  NumberX = 2
  NumberY = 1
  NumberZ = 1
  PlacementList = 2 placements: [(0,0,0),(80,0,0)]
  RadialDistance = 50
  ScaleList = (2) [(1,1,1),(1,1,1)]
  Symmetry = 1
  TangentialDistance = 25
  expr: .IntervalX.x = <<Param>>.R_Grid_Across * 2
  expr: .IntervalY.y = <<Param>>.R_Grid_Along * 2
  expr: NumberX = floor(<<Param>>.R_nof_Across / 2)
  expr: NumberY = ceil(<<Param>>.R_nof_Along / 2)
FEATURE [Sketcher::SketchObject] Sketch007
  FullyConstrained = true
  expr: Constraints[11] = <<Param>>.R_Hole_Size
  expr: Constraints[12] = <<Param>>.R_Hole_Size
  expr: Constraints[16] = <<Param>>.R_Grid_Along * (<<Param>>.R_nof_Along - 1) / 2 + <<Param>>.Heatsink_Shift
  expr: Constraints[17] = <<Param>>.R_Grid_Along
  expr: Constraints[1] = <<Param>>.Heatsink_Length / 2 - <<Param>>.R_Grid_Across * (<<Param>>.R_nof_Across - 1) / 2 - <<Param>>.R_Offset / 2
  expr: Constraints[4] = <<Param>>.R_Hole_Across
  expr: Constraints[5] = <<Param>>.R_Hole_Along
  sketch-geometry (7):
    g0: LineSegment StartX=29.4 StartY=16.15 StartZ=0 EndX=9.6 EndY=-2.15 EndZ=0
    g1: GeomPoint X=19.5 Y=7 Z=0
    g2: Circle CenterX=29.4 CenterY=16.15 CenterZ=0 NormalX=0 NormalY=0 NormalZ=1 AngleXU=0 Radius=1.25
    g3: Circle CenterX=9.6 CenterY=-2.15 CenterZ=0 NormalX=0 NormalY=0 NormalZ=1 AngleXU=0 Radius=1.25
    g4: LineSegment StartX=19.5 StartY=7 StartZ=0 EndX=29.4 EndY=16.15 EndZ=0
    g5: LineSegment StartX=19.5 StartY=7 StartZ=0 EndX=9.6 EndY=-2.15 EndZ=0
    g6: LineSegment StartX=0 StartY=-33 StartZ=0 EndX=200 EndY=-33 EndZ=0
  constraints (18):
    c: PointOnObject(g1,g0)
    c: Distance(g1,g-2) = 19.5
    c: Coincident(g0,g2)
    c: Coincident(g0,g3)
    c: DistanceX(g3,g2) = 19.8
    c: DistanceY(g3,g2) = 18.3
    c: Coincident(g4,g1)
    c: Coincident(g4,g2)
    c: Coincident(g5,g1)
    c: Coincident(g5,g3)
    c: Equal(g4,g5)
    c: Diameter(g2) = 2.5
    c: Diameter(g3) = 2.5
    c: PointOnObject(g6,g-2)
    c: Horizontal(g6)
    c: Distance(g6,g-2) = 200
    c: Distance(g6,g-1) = 33
    c: Distance(g1,g6) = 40
FEATURE [Part::Extrusion] Extrude007
  Base = -> Sketch007
  Dir = (0,0,1)
  DirMode = 2
  FaceMakerClass = Part::FaceMakerBullseye
  LengthFwd = 15
  LengthRev = 10
  Solid = true
  Symmetric = false
FEATURE [Part::FeaturePython] Array012  # Draft array (typed FeaturePython)
  AlwaysSyncPlacement = false
  Angle = 360
  ArrayType = 0
  Axis = (0,0,1)
  Base = -> Extrude007
  Center = (0,0,0)
  Count = 3
  ExpandArray = false
  Fuse = false
  IntervalAxis = (0,0,0)
  IntervalX = (80,0,0)
  IntervalY = (0,80,0)
  IntervalZ = (0,0,0)
  NumberCircles = 3
  NumberPolar = 5
  NumberX = 3
  NumberY = 1
  NumberZ = 1
  PlacementList = 3 placements: arithmetic series from (0,0,0) step (80,0,0) to (160,0,0)
  RadialDistance = 50
  ScaleList = (3) [(1,1,1),(1,1,1),(1,1,1)]
  Symmetry = 1
  TangentialDistance = 25
  expr: .IntervalX.x = <<Param>>.R_Grid_Across * 2
  expr: .IntervalY.y = <<Param>>.R_Grid_Along * 2
  expr: NumberX = ceil(<<Param>>.R_nof_Across / 2)
  expr: NumberY = floor(<<Param>>.R_nof_Along / 2)
FEATURE [Sketcher::SketchObject] Sketch008
  FullyConstrained = true
  expr: Constraints[11] = <<Param>>.R_Hole_Size
  expr: Constraints[12] = <<Param>>.R_Hole_Size
  expr: Constraints[16] = <<Param>>.R_Grid_Along * (<<Param>>.R_nof_Along - 1) / 2 + <<Param>>.Heatsink_Shift
  expr: Constraints[17] = <<Param>>.R_Grid_Along
  expr: Constraints[1] = <<Param>>.Heatsink_Length / 2 - <<Param>>.R_Grid_Across * (<<Param>>.R_nof_Across - 3) / 2 + <<Param>>.R_Offset / 2
  expr: Constraints[4] = <<Param>>.R_Hole_Across
  expr: Constraints[5] = <<Param>>.R_Hole_Along
  sketch-geometry (7):
    g0: LineSegment StartX=70.4 StartY=16.15 StartZ=0 EndX=50.6 EndY=-2.15 EndZ=0
    g1: GeomPoint X=60.5 Y=7 Z=0
    g2: Circle CenterX=70.4 CenterY=16.15 CenterZ=0 NormalX=0 NormalY=0 NormalZ=1 AngleXU=0 Radius=1.25
    g3: Circle CenterX=50.6 CenterY=-2.15 CenterZ=0 NormalX=0 NormalY=0 NormalZ=1 AngleXU=0 Radius=1.25
    g4: LineSegment StartX=60.5 StartY=7 StartZ=0 EndX=70.4 EndY=16.15 EndZ=0
    g5: LineSegment StartX=60.5 StartY=7 StartZ=0 EndX=50.6 EndY=-2.15 EndZ=0
    g6: LineSegment StartX=0 StartY=-33 StartZ=0 EndX=200 EndY=-33 EndZ=0
  constraints (18):
    c: PointOnObject(g1,g0)
    c: Distance(g1,g-2) = 60.5
    c: Coincident(g0,g2)
    c: Coincident(g0,g3)
    c: DistanceX(g3,g2) = 19.8
    c: DistanceY(g3,g2) = 18.3
    c: Coincident(g4,g1)
    c: Coincident(g4,g2)
    c: Coincident(g5,g1)
    c: Coincident(g5,g3)
    c: Equal(g4,g5)
    c: Diameter(g2) = 2.5
    c: Diameter(g3) = 2.5
    c: PointOnObject(g6,g-2)
    c: Horizontal(g6)
    c: Distance(g6,g-2) = 200
    c: Distance(g6,g-1) = 33
    c: Distance(g1,g6) = 40
FEATURE [Part::Extrusion] Extrude008
  Base = -> Sketch008
  Dir = (0,0,1)
  DirMode = 2
  FaceMakerClass = Part::FaceMakerBullseye
  LengthFwd = 15
  LengthRev = 10
  Solid = true
  Symmetric = false
FEATURE [Part::FeaturePython] Array013  # Draft array (typed FeaturePython)
  AlwaysSyncPlacement = false
  Angle = 360
  ArrayType = 0
  Axis = (0,0,1)
  Base = -> Extrude008
  Center = (0,0,0)
  Count = 2
  ExpandArray = false
  Fuse = false
  IntervalAxis = (0,0,0)
  IntervalX = (80,0,0)
  IntervalY = (0,80,0)
  IntervalZ = (0,0,0)
  NumberCircles = 3
  NumberPolar = 5
  NumberX = 2
  NumberY = 1
  NumberZ = 1
  PlacementList = 2 placements: [(0,0,0),(80,0,0)]
  RadialDistance = 50
  ScaleList = (2) [(1,1,1),(1,1,1)]
  Symmetry = 1
  TangentialDistance = 25
  expr: .IntervalX.x = <<Param>>.R_Grid_Across * 2
  expr: .IntervalY.y = <<Param>>.R_Grid_Along * 2
  expr: NumberX = floor(<<Param>>.R_nof_Across / 2)
  expr: NumberY = floor(<<Param>>.R_nof_Along / 2)
FEATURE [Part::MultiFuse] Fusion002
  Shapes = -> [Array010,Array011,Array012,Array013]
FEATURE [Sketcher::SketchObject] Sketch009
  FullyConstrained = true
  expr: Constraints[0] = <<Param>>.Heatsink_Hole
  expr: Constraints[1] = <<Param>>.Heatsink_Hole_Grid_y * (<<Param>>.Heatsink_Hole_nof_y - 1) / 2 + <<Param>>.Heatsink_Shift
  expr: Constraints[5] = <<Param>>.Heatsink_Hole_Grid_x * (<<Param>>.Heatsink_Hole_nof_x - 1) / 2
  expr: Constraints[6] = <<Param>>.Heatsink_Length / 2
  sketch-geometry (2):
    g0: Circle CenterX=10 CenterY=-58 CenterZ=0 NormalX=0 NormalY=0 NormalZ=1 AngleXU=0 Radius=1.6
    g1: LineSegment StartX=100 StartY=0 StartZ=0 EndX=100 EndY=-100 EndZ=0
  constraints (7):
    c: Diameter(g0) = 3.2
    c: Distance(g0,g-1) = 58
    c: PointOnObject(g1,g-1)
    c: Vertical(g1)
    c: Distance(g1) = 100
    c: Distance(g0,g1) = 90
    c: Distance(g1,g-2) = 100
FEATURE [Part::Extrusion] Extrude009
  Base = -> Sketch009
  Dir = (0,0,1)
  DirMode = 2
  FaceMakerClass = Part::FaceMakerBullseye
  LengthFwd = 15
  LengthRev = 10
  Solid = true
  Symmetric = false
FEATURE [Part::FeaturePython] Array014  # Draft array (typed FeaturePython)
  AlwaysSyncPlacement = false
  Angle = 360
  ArrayType = 0
  Axis = (0,0,1)
  Base = -> Extrude009
  Center = (0,0,0)
  Count = 12
  ExpandArray = false
  Fuse = false
  IntervalAxis = (0,0,0)
  IntervalX = (60,0,0)
  IntervalY = (0,45,0)
  IntervalZ = (0,0,100)
  NumberCircles = 3
  NumberPolar = 5
  NumberX = 4
  NumberY = 3
  NumberZ = 1
  PlacementList = 12 placements: [(0,0,0),(0,45,0),(0,90,0),(60,0,0),(60,45,0),(60,90,0),(120,0,0),(120,45,0),(120,90,0),(180,0,0),(180,45,0),(180,90,0)]
  RadialDistance = 50
  ScaleList = (12) [(1,1,1),(1,1,1),(1,1,1),(1,1,1),(1,1,1),(1,1,1),(1,1,1),(1,1,1),(1,1,1),(1,1,1),(1,1,1),(1,1,1)]
  Symmetry = 1
  TangentialDistance = 25
  expr: .IntervalX.x = <<Param>>.Heatsink_Hole_Grid_x
  expr: .IntervalY.y = <<Param>>.Heatsink_Hole_Grid_y
  expr: NumberX = <<Param>>.Heatsink_Hole_nof_x
  expr: NumberY = <<Param>>.Heatsink_Hole_nof_y
FEATURE [Part::FeaturePython] Array015  # Draft array (typed FeaturePython)
  AlwaysSyncPlacement = false
  Angle = 360
  ArrayType = 0
  Axis = (0,0,1)
  Base = -> Extrude009
  Center = (0,0,0)
  Count = 12
  ExpandArray = false
  Fuse = false
  IntervalAxis = (0,0,0)
  IntervalX = (60,0,0)
  IntervalY = (0,45,0)
  IntervalZ = (0,0,100)
  NumberCircles = 3
  NumberPolar = 5
  NumberX = 4
  NumberY = 3
  NumberZ = 1
  PlacementList = 12 placements: [(0,0,0),(0,45,0),(0,90,0),(60,0,0),(60,45,0),(60,90,0),(120,0,0),(120,45,0),(120,90,0),(180,0,0),(180,45,0),(180,90,0)]
  RadialDistance = 50
  ScaleList = (12) [(1,1,1),(1,1,1),(1,1,1),(1,1,1),(1,1,1),(1,1,1),(1,1,1),(1,1,1),(1,1,1),(1,1,1),(1,1,1),(1,1,1)]
  Symmetry = 1
  TangentialDistance = 25
  expr: .IntervalX.x = <<Param>>.Heatsink_Hole_Grid_x
  expr: .IntervalY.y = <<Param>>.Heatsink_Hole_Grid_y
  expr: NumberX = <<Param>>.Heatsink_Hole_nof_x
  expr: NumberY = <<Param>>.Heatsink_Hole_nof_y
FEATURE [Part::MultiFuse] Fusion003
  Shapes = -> [Fusion002,Array014]
FEATURE [PartDesign::CoordinateSystem] LCS_Origin
  AttacherType = Attacher::AttachEngine3D
  MapMode = 2
  Support = -> [X_Axis001]
FEATURE [App::DocumentObjectGroup] Constraints
FEATURE [Part::Feature] Part__Feature  label="1599K Lid"
  Placement = pos=(-35.5062,-49.1401,-2.40297) rot=(1,0,0;3.14159rad)
  shape: bbox 220 x 140 x 522.1 mm, 504 faces (baked)
FEATURE [Part::Feature] Part__Feature001  label="1599K Box"
  Placement = pos=(-35.5062,-49.1401,-3.40297) rot=(0,0,1;0rad)
  shape: bbox 220 x 140 x 525.6 mm, 228 faces (baked)
FEATURE [Part::Feature] Part__Feature002  label="SC590 (screw M3-0.5X 12mm FH)"
  Placement = pos=(-134.506,9.85994,4.35203) rot=(1,0,0;1.5708rad)
  shape: bbox 5.514 x 5.514 x 12.01 mm, 26 faces (baked)
FEATURE [Part::Feature] Part__Feature003  label="SC590 (screw M3-0.5X 12mm FH)001"
  Placement = pos=(-134.506,-108.14,4.35203) rot=(1,0,0;1.5708rad)
  shape: bbox 5.514 x 5.514 x 12.01 mm, 26 faces (baked)
FEATURE [Part::Feature] Part__Feature004  label="SC590 (screw M3-0.5X 12mm FH)002"
  Placement = pos=(63.4938,9.85994,4.35203) rot=(0.97539,-0.155908,-0.155908;1.59571rad)
  shape: bbox 5.514 x 5.514 x 12.01 mm, 26 faces (baked)
FEATURE [Part::Feature] Part__Feature005  label="SC590 (screw M3-0.5X 12mm FH)003"
  Placement = pos=(63.4938,-108.14,4.35203) rot=(1,0,0;1.5708rad)
  shape: bbox 5.514 x 5.514 x 12.01 mm, 26 faces (baked)
FEATURE [Part::Feature] Part__Feature006  label="IN100 (insert M3-0.5X5.75mm BRASS)"
  Placement = pos=(63.4938,9.85994,-6.61797) rot=(1,0,0;1.5708rad)
  shape: bbox 4.846 x 4.846 x 5.715 mm, 136 faces (baked)
FEATURE [Part::Feature] Part__Feature007  label="IN100 (insert M3-0.5X5.75mm BRASS)001"
  Placement = pos=(-134.506,9.85994,-6.61797) rot=(1,0,0;1.5708rad)
  shape: bbox 4.846 x 4.846 x 5.715 mm, 136 faces (baked)
FEATURE [Part::Feature] Part__Feature008  label="IN100 (insert M3-0.5X5.75mm BRASS)002"
  Placement = pos=(63.4938,-108.14,-6.61797) rot=(1,0,0;1.5708rad)
  shape: bbox 4.846 x 4.846 x 5.715 mm, 136 faces (baked)
FEATURE [Part::Feature] Part__Feature009  label="IN100 (insert M3-0.5X5.75mm BRASS)003"
  Placement = pos=(-134.506,-108.14,-6.61797) rot=(1,0,0;1.5708rad)
  shape: bbox 4.846 x 4.846 x 5.715 mm, 136 faces (baked)
FEATURE [App::Part] _599K  label="1599K"
  Group = -> [Part__Feature,Part__Feature001,Part__Feature002,Part__Feature003,Part__Feature004,Part__Feature005,Part__Feature006,Part__Feature007,Part__Feature008,Part__Feature009]
  Origin = -> Origin
  Placement = pos=(135,-49.14,-32.403) rot=(1,0,0;3.14159rad)
FEATURE [Part::Cut] Cut
  Base = -> _599K
  Tool = -> Fusion001
FEATURE [Part::Cut] Cut002  label="Housing_milled"
  Base = -> Cut
  Tool = -> Array015
FEATURE [Part::Feature] Part__Feature011  label="10021079"
  Placement = pos=(5,48,-21) rot=(0,0,1;0rad)
  shape: bbox 15.72 x 15.72 x 32.42 mm, 532 faces, 2 solids (baked)
  expr: .Placement.Base.x = <<Param>>.Heatsink_Length / 2 - <<Param>>.Con_Grid * (<<Param>>.Con_nof - 1) / 2
  expr: .Placement.Base.y = <<Param>>.Con_Pos_y
FEATURE [Part::FeaturePython] Array  label="Connectors"  # Draft array (typed FeaturePython)
  Angle = 360
  ArrayType = 0
  Axis = (0,0,1)
  Base = -> Part__Feature011
  Center = (0,0,0)
  Fuse = false
  IntervalAxis = (0,0,0)
  IntervalX = (19,0,0)
  IntervalY = (0,-100,0)
  IntervalZ = (0,0,1)
  NumberPolar = 1
  NumberX = 11
  NumberY = 1
  NumberZ = 1
  expr: .IntervalX.x = <<Param>>.Con_Grid
FEATURE [Part::Feature] Part__Feature010  label="SK047"
  Placement = pos=(0,0,0) rot=(1,0,0;1.5708rad)
  shape: bbox 200 x 10 x 40 mm, 124 faces (baked)
FEATURE [Part::FeaturePython] Scale001  label="SK47-100"  # Draft clone (typed FeaturePython)
  AssemblyType = Part::Link
  AttachedBy = Origin
  AttachedTo = Parent Assembly#LCS_Origin
  AttachmentOffset = pos=(0,37,0) rot=(1,0,0;1.5708rad)
  Fuse = false
  Objects = -> [Part__Feature010]
  Placement = pos=(0,37,0) rot=(1,0,0;1.5708rad)
  Scale = (1,1,10)
  SolverId = Asm4EE
  expr: Placement = LCS_Origin.Placement * AttachmentOffset
FEATURE [Part::Cut] Cut001  label="Heatsink_drilled"
  Base = -> Scale001
  Tool = -> Fusion003
FEATURE [App::DocumentObjectGroup] Configurations
FEATURE [App::FeaturePython] Variables  # WARN: FeaturePython — macro-defined, semantics opaque (R4)
  Type = App::PropertyContainer
FEATURE [App::Part] Model
  AssemblyType = Part::Link
  Group = -> [LCS_Origin,Constraints,Variables,Configurations,Scale001,_599K,Part__Feature011,Array,Part__Feature010]
  Origin = -> Origin001
  Type = Assembly
